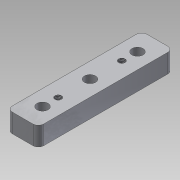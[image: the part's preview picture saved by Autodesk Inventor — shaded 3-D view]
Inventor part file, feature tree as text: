
AUTODESK INVENTOR PART (.ipt)
format: ipt  version: 2013 SP2 (Build 170200200, 200)  size: 98,816 bytes
history: native  units: mm
features: sketch x3, hole x2, extrude x1, fillet x1
ambient origin geometry x8: Origin, YZ Plane, XZ Plane, XY Plane, X Axis, Y Axis, Z Axis, Center Point
bodies: Solid1 (feature_tree)
feature tree (7):
  extrude  "Extrusion1"  Depth=86.04mm
  hole  "Hole1"  [1 undecoded]
  hole  "Hole2"  [1 undecoded]
  fillet  "Fillet1"  Radius=20.32mm
  sketch  "Sketch1"  dims[d0=20.0mm d1=86.04mm]
  sketch  "Sketch2"  dims[d2=12.0mm d3=0.0mm d4=30.32mm]
  sketch  "Sketch3"  dims[d5=30.32mm d6=7.14mm d7=6.0mm d8=4.0mm d9=2.0mm d10=90.0deg d11=8.0mm d12=20.594885mm d13=20.32mm d14=20.32mm d15=4.134mm d16=12.0mm d17=4.0mm d18=2.0mm d19=90.0deg d20=8.0mm d21=20.594885mm d22=3.36mm]
note: 2 required parameter values undecoded (feature->parameter linkage not recoverable at this tier; creation-order binding heuristic only, values carry confidence <= 0.55)
